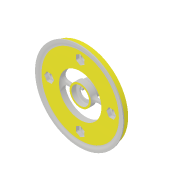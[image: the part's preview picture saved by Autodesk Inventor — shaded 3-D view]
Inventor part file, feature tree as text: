
AUTODESK INVENTOR PART (.ipt)
format: ipt  version: 2018 (Build 220112000, 112)  size: 688,640 bytes
history: native  units: in
note: dims shown in document units (in); Inventor stores cm internally (conversion verified against a paired STEP export)
features: sketch x14, extrude x13, fillet x8, pattern_circular x2, plane x1, mirror x1, revolve x1, projected_geometry x1
ambient origin geometry x8: Origin, YZ Plane, XZ Plane, XY Plane, X Axis, Y Axis, Z Axis, Center Point
bodies: Solid1 (feature_tree)
feature tree (41):
  extrude  "Extrusion1"  Depth=0.25in
  extrude  "Extrusion2"  Depth=0.65in
  extrude  "Extrusion3"  Depth=0.0394in
  extrude  "Extrusion4"  Depth=0.495in TaperAngle=0.0deg
  extrude  "Extrusion5"  Depth=0.0591in TaperAngle=0.0deg
  plane  "Work Plane1"
  extrude  "Extrusion6"  Depth=0.0394in TaperAngle=0.0deg
  mirror  "Mirror1"
  revolve  "Revolution1"  [1 undecoded]
  fillet  "Fillet1"  Radius=0.1908in
  extrude  "Extrusion8"  Depth=0.2756in
  fillet  "Fillet3"  Radius=0.6412in
  extrude  "Extrusion9"  Depth=0.2234in TaperAngle=0.0deg
  extrude  "Extrusion10"  Depth=0.0394in
  fillet  "Fillet4"  Radius=0.0394in
  fillet  "Fillet5"  Radius=0.0625in
  extrude  "Extrusion11"  Depth=0.125in
  fillet  "Fillet6"  Radius=1.5in
  extrude  "Extrusion12"  Depth=0.4125in
  extrude  "Extrusion13"  Depth=0.125in
  pattern_circular  "Circular Pattern2"  [2 undecoded]
  pattern_circular  "Circular Pattern3"  [2 undecoded]
  extrude  "Extrusion14"  Depth=0.1575in TaperAngle=0.0deg
  fillet  "Fillet7"  Radius=0.025in
  fillet  "Fillet8"  Radius=0.02in
  fillet  "Fillet9"  Radius=0.75in
  sketch  "Sketch1"  dims[d0=3.0in d2=0.25in]
  sketch  "Sketch2"  dims[d3=0.1969in d4=0.0in d7=0.65in]
  sketch  "Sketch3"  dims[d8=0.27in d9=0.0394in]
  sketch  "Sketch4"  dims[d10=0.0197in d11=0.495in d12=0.0in]
  sketch  "Sketch5"  dims[d13=0.0394in d14=0.0591in d15=0.0in]
  sketch  "Sketch6"  dims[d16=0.0394in d17=0.0in d18=0.0394in d19=0.0in]
  sketch  "Sketch7"  dims[d20=0.0866in d21=0.0954in d22=0.1908in]
  sketch  "Sketch9"  dims[d23=0.2672in d24=0.2756in d25=0.6412in d26=0.0in]
  sketch  "Sketch10"  dims[d27=-0.35in d29=0.2234in d30=0.0in]
  sketch  "Sketch11"  dims[d31=0.65in d32=0.0394in d33=0.0394in d34=0.0625in]
  projected_geometry  "Projected Loop1"
  sketch  "Sketch12"  dims[d35=90.0deg d36=0.125in d37=1.5in d38=0.75in]
  sketch  "Sketch13"  dims[d48=0.5344in d49=0.4125in]
  sketch  "Sketch14"  dims[d50=0.1969in d51=0.0in d52=0.125in]
  sketch  "Sketch15"  dims[d53=0.625in d54=0.2106in d55=0.0in d57=0.3937in d58=0.0394in d59=0.0in d60=0.025in d61=0.02in d62=0.75in d63=1.5in d64=0.0481in d65=1.0in d66=0.0in d67=0.125in d68=0.1772in d69=1.1in d70=1.1in d71=1.0in d72=0.0in d76=0.13in d78=0.1181in d79=0.0in d80=1.5748in d81=360.0deg d83=1.5748in d84=360.0deg d86=0.2953in d87=0.1654in d88=0.1181in d89=0.0in d90=0.125in d91=0.0512in d92=0.1575in]
note: 5 required parameter values undecoded (feature->parameter linkage not recoverable at this tier; creation-order binding heuristic only, values carry confidence <= 0.55)